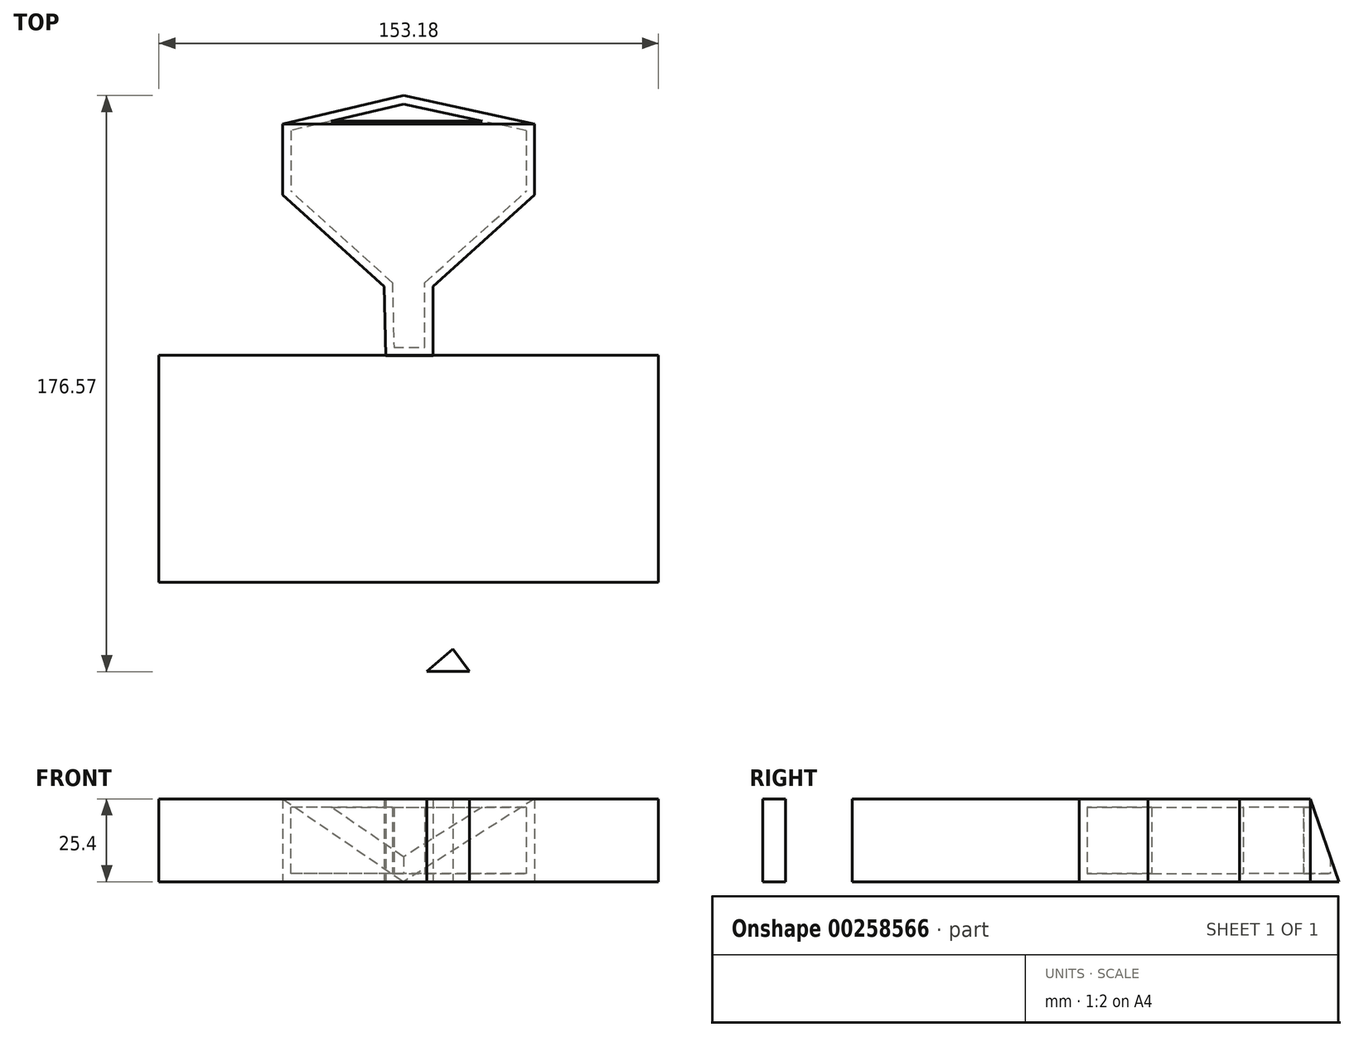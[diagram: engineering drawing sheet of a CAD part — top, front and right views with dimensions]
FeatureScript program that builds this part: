
annotation { "Feature Type Name" : "Feature", "Feature Type Description" : "" }
export const myFeature = defineFeature(function(context is Context, id is Id, definition is map)
    precondition{}
    {
        {
            var Q0;
            Q0=qCreatedBy(makeId("Top.planeOp"),FACE);
            var sketch = newSketch(context, id + "F0", { "sketchPlane" : qUnion([Q0])});
            skPoint(sketch, "E0", {"position": v(147.3, 111.2) * mm});
            skLineSegment(sketch, "E1.bottom", {"start": v(-75.51, -4.25) * mm, "end": v(77.67, -4.25) * mm});
            skLineSegment(sketch, "E1.top", {"start": v(-75.51, -73.86) * mm, "end": v(77.67, -73.86) * mm});
            skLineSegment(sketch, "E1.left", {"start": v(-75.51, -4.25) * mm, "end": v(-75.51, -73.86) * mm});
            skLineSegment(sketch, "E1.right", {"start": v(77.67, -4.25) * mm, "end": v(77.67, -73.86) * mm});
            skLineSegment(sketch, "E2.bottom", {"start": v(-67.8, -137.41) * mm, "end": v(-66.06, -137.41) * mm});
            skLineSegment(sketch, "E2.top", {"start": v(-67.8, -162.81) * mm, "end": v(-66.06, -162.81) * mm});
            skLineSegment(sketch, "E2.left", {"start": v(-67.8, -137.41) * mm, "end": v(-67.8, -162.81) * mm});
            skLineSegment(sketch, "E2.right", {"start": v(-66.06, -137.41) * mm, "end": v(-66.06, -162.81) * mm});
            skLineSegment(sketch, "E3.bottom", {"start": v(-66.06, -137.41) * mm, "end": v(-59, -137.41) * mm});
            skLineSegment(sketch, "E3.top", {"start": v(-66.06, -139.22) * mm, "end": v(-59, -139.22) * mm});
            skLineSegment(sketch, "E3.left", {"start": v(-66.06, -137.41) * mm, "end": v(-66.06, -139.22) * mm});
            skLineSegment(sketch, "E3.right", {"start": v(-59, -137.41) * mm, "end": v(-59, -139.22) * mm});
            skLineSegment(sketch, "E4.bottom", {"start": v(-66.06, -147.43) * mm, "end": v(-61.02, -147.43) * mm});
            skLineSegment(sketch, "E4.top", {"start": v(-66.06, -149.09) * mm, "end": v(-61.02, -149.09) * mm});
            skLineSegment(sketch, "E4.left", {"start": v(-66.06, -147.43) * mm, "end": v(-66.06, -149.09) * mm});
            skLineSegment(sketch, "E4.right", {"start": v(-61.02, -147.43) * mm, "end": v(-61.02, -149.09) * mm});
            skLineSegment(sketch, "E5.bottom", {"start": v(-66.06, -160.05) * mm, "end": v(-59.4, -160.05) * mm});
            skLineSegment(sketch, "E5.top", {"start": v(-66.06, -162.81) * mm, "end": v(-59.4, -162.81) * mm});
            skLineSegment(sketch, "E5.left", {"start": v(-66.06, -160.05) * mm, "end": v(-66.06, -162.81) * mm});
            skLineSegment(sketch, "E5.right", {"start": v(-59.4, -160.05) * mm, "end": v(-59.4, -162.81) * mm});
            skLineSegment(sketch, "E6.bottom", {"start": v(-43.03, -82.63) * mm, "end": v(-39.76, -82.63) * mm});
            skLineSegment(sketch, "E6.top", {"start": v(-43.03, -106.07) * mm, "end": v(-39.76, -106.07) * mm});
            skLineSegment(sketch, "E6.left", {"start": v(-43.03, -82.63) * mm, "end": v(-43.03, -106.07) * mm});
            skLineSegment(sketch, "E6.right", {"start": v(-39.76, -82.63) * mm, "end": v(-39.76, -106.07) * mm});
            skLineSegment(sketch, "E7.bottom", {"start": v(-46.72, -82.63) * mm, "end": v(-34.53, -82.63) * mm});
            skLineSegment(sketch, "E7.top", {"start": v(-46.72, -80.67) * mm, "end": v(-34.53, -80.67) * mm});
            skLineSegment(sketch, "E7.left", {"start": v(-46.72, -82.63) * mm, "end": v(-46.72, -80.67) * mm});
            skLineSegment(sketch, "E7.right", {"start": v(-34.53, -82.63) * mm, "end": v(-34.53, -80.67) * mm});
            skLineSegment(sketch, "E8.bottom", {"start": v(-26.55, -107.12) * mm, "end": v(-22.98, -107.12) * mm});
            skLineSegment(sketch, "E8.top", {"start": v(-26.55, -132.52) * mm, "end": v(-22.98, -132.52) * mm});
            skLineSegment(sketch, "E8.left", {"start": v(-26.55, -107.12) * mm, "end": v(-26.55, -132.52) * mm});
            skLineSegment(sketch, "E8.right", {"start": v(-22.98, -107.12) * mm, "end": v(-22.98, -132.52) * mm});
            skLineSegment(sketch, "E9.bottom", {"start": v(-22.98, -123.76) * mm, "end": v(-15.95, -123.76) * mm});
            skLineSegment(sketch, "E9.top", {"start": v(-22.98, -126.25) * mm, "end": v(-15.95, -126.25) * mm});
            skLineSegment(sketch, "E9.left", {"start": v(-22.98, -123.76) * mm, "end": v(-22.98, -126.25) * mm});
            skLineSegment(sketch, "E9.right", {"start": v(-15.95, -123.76) * mm, "end": v(-15.95, -126.25) * mm});
            skLineSegment(sketch, "E10.bottom", {"start": v(-15.95, -123.76) * mm, "end": v(-14.12, -123.76) * mm});
            skLineSegment(sketch, "E10.top", {"start": v(-15.95, -138) * mm, "end": v(-14.12, -138) * mm});
            skLineSegment(sketch, "E10.left", {"start": v(-15.95, -123.76) * mm, "end": v(-15.95, -138) * mm});
            skLineSegment(sketch, "E10.right", {"start": v(-14.12, -123.76) * mm, "end": v(-14.12, -138) * mm});
            skLineSegment(sketch, "E11", {"start": v(-0.71, -110.4) * mm, "end": v(14.62, -90.15) * mm});
            skLineSegment(sketch, "E12", {"start": v(14.62, -90.15) * mm, "end": v(14.62, -94.28) * mm});
            skLineSegment(sketch, "E13", {"start": v(14.62, -94.28) * mm, "end": v(-5.5, -111.88) * mm});
            skLineSegment(sketch, "E14", {"start": v(-5.5, -111.88) * mm, "end": v(-0.71, -110.4) * mm});
            skLineSegment(sketch, "E15", {"start": v(14.62, -90.15) * mm, "end": v(29.47, -110.4) * mm});
            skLineSegment(sketch, "E16", {"start": v(14.62, -94.28) * mm, "end": v(27.52, -111.88) * mm});
            skLineSegment(sketch, "E17", {"start": v(27.52, -111.88) * mm, "end": v(29.47, -110.4) * mm});
            skLineSegment(sketch, "E18", {"start": v(6.67, -101.24) * mm, "end": v(19.72, -101.24) * mm});
            skLineSegment(sketch, "E19", {"start": v(19.72, -101.24) * mm, "end": v(21.07, -103.08) * mm});
            skLineSegment(sketch, "E20", {"start": v(21.07, -103.08) * mm, "end": v(4.56, -103.08) * mm});
            skLineSegment(sketch, "E21", {"start": v(4.56, -103.08) * mm, "end": v(6.67, -101.24) * mm});
            skLineSegment(sketch, "E22.bottom", {"start": v(37.68, -123.25) * mm, "end": v(42.74, -123.25) * mm});
            skLineSegment(sketch, "E22.top", {"start": v(37.68, -97.85) * mm, "end": v(42.74, -97.85) * mm});
            skLineSegment(sketch, "E22.left", {"start": v(37.68, -123.25) * mm, "end": v(37.68, -97.85) * mm});
            skLineSegment(sketch, "E22.right", {"start": v(42.74, -123.25) * mm, "end": v(42.74, -97.85) * mm});
            skLineSegment(sketch, "E23.bottom", {"start": v(42.74, -97.85) * mm, "end": v(58.63, -97.85) * mm});
            skLineSegment(sketch, "E23.top", {"start": v(42.74, -101.49) * mm, "end": v(58.63, -101.49) * mm});
            skLineSegment(sketch, "E23.left", {"start": v(42.74, -97.85) * mm, "end": v(42.74, -101.49) * mm});
            skLineSegment(sketch, "E23.right", {"start": v(58.63, -97.85) * mm, "end": v(58.63, -101.49) * mm});
            skLineSegment(sketch, "E24.bottom", {"start": v(58.63, -97.85) * mm, "end": v(62.48, -97.85) * mm});
            skLineSegment(sketch, "E24.top", {"start": v(58.63, -123.25) * mm, "end": v(62.48, -123.25) * mm});
            skLineSegment(sketch, "E24.left", {"start": v(58.63, -97.85) * mm, "end": v(58.63, -123.25) * mm});
            skLineSegment(sketch, "E24.right", {"start": v(62.48, -97.85) * mm, "end": v(62.48, -123.25) * mm});
            skLineSegment(sketch, "E25", {"start": v(-64.32, -62.12) * mm, "end": v(-64.32, -24.6) * mm});
            skLineSegment(sketch, "E26", {"start": v(-64.32, -24.6) * mm, "end": v(-64.32, -43.36) * mm});
            skLineSegment(sketch, "E27", {"start": v(-64.32, -43.36) * mm, "end": v(-64.32, -24.6) * mm});
            skLineSegment(sketch, "E28", {"start": v(-46.76, -33.98) * mm, "end": v(-64.32, -33.98) * mm});
            skPoint(sketch, "E28.startSnap0", {"position": v(-64.32, -33.98) * mm});
            skLineSegment(sketch, "E29", {"start": v(-64.32, -33.98) * mm, "end": v(-46.76, -33.98) * mm});
            skSolve(sketch);
        }
        {
            var Q0;
            Q0=qCreatedBy(makeId("Top.planeOp"),FACE);
            var sketch = newSketch(context, id + "F1", { "sketchPlane" : qUnion([Q0])});
            skLineSegment(sketch, "E30", {"start": v(-5.93, -4.4) * mm, "end": v(8.59, -4.4) * mm});
            skLineSegment(sketch, "E31", {"start": v(8.59, -4.4) * mm, "end": v(8.59, 16.85) * mm});
            skLineSegment(sketch, "E32", {"start": v(8.59, 16.85) * mm, "end": v(-6.44, 16.85) * mm});
            skLineSegment(sketch, "E33", {"start": v(-6.44, 16.85) * mm, "end": v(-5.93, -4.4) * mm});
            skLineSegment(sketch, "E34", {"start": v(8.59, 16.85) * mm, "end": v(39.7, 44.85) * mm});
            skLineSegment(sketch, "E35", {"start": v(39.7, 44.85) * mm, "end": v(24.14, 30.85) * mm});
            skLineSegment(sketch, "E36", {"start": v(24.14, 30.85) * mm, "end": v(39.7, 44.85) * mm});
            skLineSegment(sketch, "E37", {"start": v(-6.44, 16.85) * mm, "end": v(-37.55, 44.85) * mm});
            skLineSegment(sketch, "E38", {"start": v(-37.55, 44.85) * mm, "end": v(39.7, 44.85) * mm});
            skLineSegment(sketch, "E39.bottom", {"start": v(-37.55, 66.62) * mm, "end": v(39.7, 66.62) * mm});
            skLineSegment(sketch, "E39.left", {"start": v(-37.55, 66.62) * mm, "end": v(-37.55, 44.85) * mm});
            skLineSegment(sketch, "E39.right", {"start": v(39.7, 66.62) * mm, "end": v(39.7, 44.85) * mm});
            skSolve(sketch);
        }
        {
            var Q0;
            Q0=makeQuery(id+"F1.imprint","IMPRINT",FACE,{"disambiguationData":[TD([[makeQuery(id+"F1.imprint","IMPRINT",EDGE,{"derivedFrom":sQuery(id+"F1.wireOp",EDGE,"E39.bottom")}),-1.0]])]});
            var Q1;
            Q1=makeQuery(id+"F1.imprint","IMPRINT",FACE,{"disambiguationData":[TD([[makeQuery(id+"F1.imprint","IMPRINT",EDGE,{"derivedFrom":sQuery(id+"F1.wireOp",EDGE,"E32")}),-1.0]])]});
            var Q2;
            Q2=makeQuery(id+"F1.imprint","IMPRINT",FACE,{"disambiguationData":[TD([[makeQuery(id+"F1.imprint","IMPRINT",EDGE,{"derivedFrom":sQuery(id+"F1.wireOp",EDGE,"E30")}),1.0]])]});
            var Q3;
            Q3=makeQuery(id+"F0.imprint","IMPRINT",FACE,{"disambiguationData":[TD([[makeQuery(id+"F0.imprint","IMPRINT",EDGE,{"derivedFrom":sQuery(id+"F0.wireOp",EDGE,"E1.bottom")}),-1.0]])]});
            var Q4;
            {var subQ3=sQuery(id+"F0.wireOp",EDGE,"E18");Q4=makeQuery(id+"F0.imprint","IMPRINT",FACE,{"disambiguationData":[TD([[makeQuery(id+"F0.imprint","IMPRINT",EDGE,{"derivedFrom":subQ3}),1.0]])]});}
            extrude(context, id + "F2", {"entities" : qUnion([Q0, Q1, Q2, Q3, Q4]), "depth" : 25.4 * mm});
        }
        {
            var Q0;
            Q0=qCreatedBy(makeId("Top.planeOp"),FACE);
            var sketch = newSketch(context, id + "F3", { "sketchPlane" : qUnion([Q0])});
            skFitSpline(sketch, "E40", {"points": [v(-37.67, 66.98) * mm, v(-30.99, 72.4) * mm, v(-0.52, 75.33) * mm, v(33.71, 73.66) * mm, v(39.97, 66.98) * mm], "startDerivative": vector(30.25, 36.28) * mm, "endDerivative": vector(24.25, -44.2) * mm});
            skSolve(sketch);
        }
        {
            var Q1;
            Q1=makeQuery(id+"F2.opExtrude","SWEPT_FACE",FACE,{"disambiguationData":[OSD([sQuery(id+"F1.wireOp",EDGE,"E39.bottom")])]});
            var Q2;
            Q2=sQuery(id+"F3.wireOp",VERTEX,"E40.2.internal");
            loft(context, id + "F4", {"operationType" : NewBodyOperationType.ADD, "sheetProfilesArray" : [{ "sheetProfileEntities" : qUnion([Q1]) }, { "sheetProfileEntities" : qUnion([Q2]) }]});
        }
        {
            var Q0;
            {var subQ0=sQuery(id+"F1.wireOp",EDGE,"E39.bottom");var subQ1=sQuery(id+"F1.wireOp",EDGE,"E39.right");var subQ2=sQuery(id+"F1.wireOp",EDGE,"E39.left");Q0=makeQuery(id+"F4.opLoft","SWEPT_FACE",FACE,{"disambiguationData":[OSD([subQ0,subQ2,subQ1]),TDD([makeQuery(id+"F2.opExtrude","CAP_VERTEX",VERTEX,{"disambiguationData":[OSD([subQ0,subQ2])],"isStart":false}),makeQuery(id+"F2.opExtrude","CAP_VERTEX",VERTEX,{"disambiguationData":[OSD([subQ0,subQ1])],"isStart":false}),makeQuery(id+"F2.opExtrude","CAP_EDGE",EDGE,{"disambiguationData":[OSD([subQ0])],"isStart":false})])]});}
            shell(context, id + "F5", {"entities" : qUnion([Q0]), "thickness" : 2.54 * mm});
        }
    });
